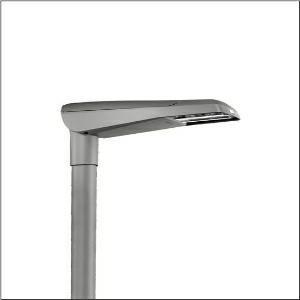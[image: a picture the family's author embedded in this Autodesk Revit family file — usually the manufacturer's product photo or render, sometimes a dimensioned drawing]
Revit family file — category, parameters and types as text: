
# Revit family: streetlight_sl_11_iq_micro___st1_0ab_5xc1nc1f08de_8c0d
name_source: partatom
category: Lighting Fixtures
units: mm (PartAtom-declared; Revit-internal decimal feet)

## family parameters
Cut with Voids When Loaded = No
Host = Face
Light Source = No
Part Type = Normal
Room Calculation Point = No
Round Connector Dimension = Use Diameter
Shared = No

## types (1)
- --- (1 x LED, 3090 lm, 27.4 W, 4000K)
    Apparent Load = 27 VA
    CIE Flux Codes = 29 63 95 100 100
    Color Rendering = 70
    Color Temperature = 4000K
    Default Elevation = 1800 mm
    Description = Streetlight SL 11 iQ micro, mast luminaire, primary light control with 3 zone facetted reflector, of plastic, silver coated, highly specular, primary optical cover: cover, of PMMA, transparent, light distribution: ST1.0aB, light emission: direct distribution, primary light characteristic: asymmetric, installation type: post-top, side-entry, lamps: LED, High Power LED, rated values: 2.900lm | 27,7W | 104,7lm/W (begin service life); end service life: 2.900lm | 28,1W; at 50% lumin. flux: 1.450lm | 13,4W | 108,2lm/W, colour temperature: 2200/2700/3000/4000K, colour rendering: CRI > 70, light colour: 722/727/730/740, light setting 1 begin service life: 100% | 2.900lm | 27,7W | 104,7lm/W | 3.000K, light setting 1 end service life: 28,1W, further light settings possible, control: Street-Remote, Auto-Match, Temp-Guard, Lumen-Switch, Night-Set, Smart-Wire, Light-Fading, Desk-Remote (wireless, voltage-free reading and setting of iQ features in the workshop via application-optimized NFC function/RFID function), optimised constant luminous flux control (CLO 2.0), with cable H07RN-F 3x 1.5mm², mains connection: 220..240V, AC, 50/60Hz, connection cable pre-assembled, cable length: 6,5m, luminaire housing, of diecast aluminium, powder-coated, SITECO metallic grey (DB 702S), please order mast flange separately, inclination adjustable without tools: 0°, 5°, 10°, 15° (post-top) | 0°, -5°, -10°, -15° (side-entry), sealing non-destructively replaceable, multi-level sealing system, length: 600mm, width: 174mm, height: 116mm, mast flange for spigot size: 42mm (side-entry): 5XC10008XM4, 60/48mm (side-entry/post-top): 5XC10108XM2, 76/60mm (side-entry/post-top): 5XC10108XM1, equipment: Power, protection rating (complete): IP66, insulation class (complete): insulation class II (safety insulation), certification: CE, ENEC, ENEC+, VDE, impact resistance: IK10, permissible operating ambient temperature for outdoor applications: -25..+50°C, standard-compliant lighting for roads and squares, Environmental Product Declaration (EPD) tested and certified by an independent institute, packaging unit: 1 piece

Light Distribution: ST1.0aB
    Height = 116 mm
    Lamp = 1 x LED
    Lamp Light Flux = 3090 lm
    Lamp Power = 27.4 W
    Lamp count = 1
    Length = 600 mm
    Luminous efficacy = 113 lm/W
    Manufacturer = Siteco
    ModVariant = No
    Model = 5XC1NC1F08DE
    Number of Poles = 1
    OnlyDefault = Yes
    Power Factor = 1
    Product Name = Streetlight SL 11 iQ micro | ST1.0aB
    Product group = mast luminaire | pylon top
    ProductGroupID = 6100
    Protection Class = Protection class II
    Protection Degree = IP 66
    RLX_Detail_Level = 1
    RLX_Emergency_Light_Flux = 0 lm
    RLX_Emergency_Type = 0
    RLX_Emergency_Type_DB = No
    RlxData = <blob elided: 59329 chars, md5=a5c236ed>
    Socket = socket
    Standby Power = 0 W
    System Light Flux = 3090 lm
    System Power = 27 W
    Type Comments = individual setting: luminous flux: 100 % | dim-lin: 254 | 726 mA
    Type Image = l_1006566.jpg
    URL = http://relux.com
    VarID = @adj_021119
    Voltage = 0 V
    Weight = 0.00 kg
    Width = 174 mm

## geometry (parser evidence)
native form markers: Blend x4, Sweep x12
no freeform markers — native parametric forms only
